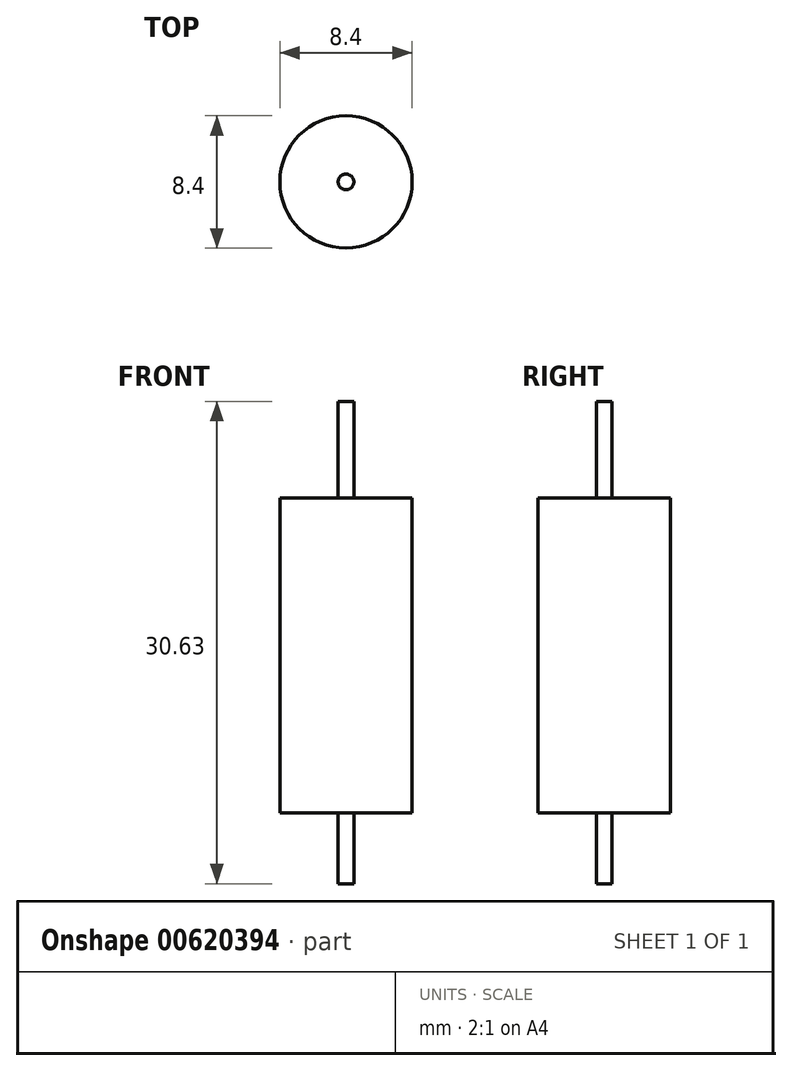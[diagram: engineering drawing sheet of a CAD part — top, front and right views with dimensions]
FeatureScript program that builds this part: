
annotation { "Feature Type Name" : "Feature", "Feature Type Description" : "" }
export const myFeature = defineFeature(function(context is Context, id is Id, definition is map)
    precondition{}
    {
        {
            var Q0;
            Q0=qCreatedBy(makeId("Top.planeOp"),FACE);
            var sketch = newSketch(context, id + "F0", { "sketchPlane" : qUnion([Q0])});
            skCircle(sketch, "E0", {"center": v(0, 0) * mm, "radius": 4.2 * mm});
            skSolve(sketch);
        }
        {
            var Q0;
            Q0=qSketchRegion(id+"F0",true);
            extrude(context, id + "F1", {"entities" : qUnion([Q0]), "depth" : 20 * mm});
        }
        {
            var Q0;
            Q0=makeQuery(id+"F1.opExtrude","CAP_FACE",FACE,{"disambiguationData":[OSD([sQuery(id+"F0.wireOp",EDGE,"E0")])],"isStart":true});
            var sketch = newSketch(context, id + "F2", { "sketchPlane" : qUnion([Q0])});
            skCircle(sketch, "E1", {"center": v(0, 0) * mm, "radius": 0.5 * mm});
            skSolve(sketch);
        }
        {
            var Q0;
            Q0=qSketchRegion(id+"F2",true);
            extrude(context, id + "F3", {"entities" : qUnion([Q0]), "operationType" : NewBodyOperationType.ADD, "depth" : 4.5 * mm});
        }
        {
            var Q0;
            Q0=makeQuery(id+"F3.opExtrude","CAP_FACE",FACE,{"disambiguationData":[OSD([sQuery(id+"F2.wireOp",EDGE,"E1")])],"isStart":false});
            var sketch = newSketch(context, id + "F4", { "sketchPlane" : qUnion([Q0])});
            skSolve(sketch);
        }
        {
            var Q0;
            Q0=makeQuery(id+"F4.imprint","IMPRINT",FACE,{"disambiguationData":[TD([[makeQuery(id+"F4.imprint","IMPRINT",EDGE,{"derivedFrom":makeQuery(id+"F3.opExtrude","CAP_EDGE",EDGE,{"disambiguationData":[OSD([sQuery(id+"F2.wireOp",EDGE,"E1")])],"isStart":false})}),1.0]])]});
            extrude(context, id + "F5", {"entities" : qUnion([Q0]), "operationType" : NewBodyOperationType.ADD, "oppositeDirection" : true, "depth" : 30.63 * mm});
        }
    });
